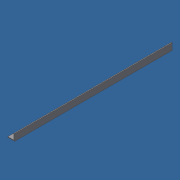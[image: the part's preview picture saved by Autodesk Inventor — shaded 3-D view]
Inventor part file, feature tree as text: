
AUTODESK INVENTOR PART (.ipt)
format: ipt  version: 2021 (Build 250183000, 183)  size: 77,312 bytes
history: native  units: mm
features: extrude x1, sketch x1
ambient origin geometry x8: Origin, YZ Plane, XZ Plane, XY Plane, X Axis, Y Axis, Z Axis, Center Point
bodies: Solid1 (feature_tree)
feature tree (2):
  extrude  "Extrusion1"  Depth=20.0mm
  sketch  "Sketch1"  dims[d0=20.0mm d1=20.0mm d2=2.0mm d3=2.0mm d4=465.0mm d5=0.0mm]
